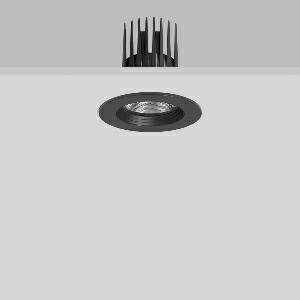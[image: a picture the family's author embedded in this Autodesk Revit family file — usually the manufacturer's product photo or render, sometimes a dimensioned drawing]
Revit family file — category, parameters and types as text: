
# Revit family: heledon_mini_e_901741_003_1376
name_source: partatom
category: Lighting Fixtures
units: mm (PartAtom-declared; Revit-internal decimal feet)

## family parameters
Cut with Voids When Loaded = No
Host = Face
Light Source = No
Part Type = Normal
Room Calculation Point = No
Round Connector Dimension = Use Diameter
Shared = No

## types (1)
- HELEDON mini E (1 x LED Modul 930, 2450 lm, 3000)
    Apparent Load = 20 VA
    Approval mark = CE
    CIE Flux Codes = 99 100 100 100 100
    Color Rendering = 90
    Color Temperature = 3000
    Default Elevation = 1800 mm
    Description = Series: HELEDON mini
Round recessed downlight. Housing: die-cast aluminium, powder-coated. Black plastic ring and recessed LED to prevent glare from the side. Optical assembly with reflector made of MIRO-Silver with 98% total light reflection for outstanding efficiency - can be changed without tools. Best colour rendering index Ra>90. Suitable for Recessed ceiling mounting. Installation without tools thanks to spring fastening system. Including separate LED converter with connecting cable 600 mm.High quality converter without flickering and stroboscopic effect. Through-wiring box (5 pole) available as accessory. The following accessories can be mounted without use of tools: interchangeable lenses, decorative glasses, honeycomb louvre, clear and frosted diffusers, white interchangeable plastic ring. 
Colour: deep black, matt (RAL 9005)
Diameter: 124 mm
Height: 3 mm
Cut-out diameter: 114 mm
Recess height: 170 mm
Luminaire: recess height: 120 mm
Lamp: LED
Socket: without socket
Colour temperature: 3000K
Colour rendering index (CRI): 92
System power: 20 W
Rated luminous flux: 2450 lm
Luminous efficiency: 123 lm/W
Control gear: Regulated power supply
Protection class: II
Type of protection: IP 20
    Height = 0 mm  [stored 0 ft]
    Lamp = 1 x LED Modul 930
    Lamp Light Flux = 2450 lm
    Lamp count = 1
    Length = 124 mm  [stored 0.406824 ft]
    Lifetime = 50000 h
    Luminous efficacy = 123 lm/W
    Manufacturer = RZB
    ModVariant = No
    Model = 901741.003
    Mounting Place = Ceiling
    Mounting Type = Recessed
    Number of Poles = 1
    OnlyDefault = Yes
    Power Factor = 1
    Product Name = HELEDON mini E
    Product group = Recessed downlights
    ProductGroupID = 402
    Protection Class = Protection class II
    Protection Degree = IP 20
    RLX_Detail_Level = 1
    RLX_Emergency_Light_Flux = 0 lm
    RLX_Emergency_Type = 0
    RLX_Emergency_Type_DB = No
    RlxData = <blob elided: 127377 chars, md5=e48d8572>
    Socket = socket
    Standby Power = 0 W
    System Light Flux = 2450 lm
    System Power = 20 W
    Type Comments = Product without accessories
    Type Image = 901657.003.jpg
    URL = http://relux.com
    VarID = ---
    Voltage = 230 V
    Voltage Range = 220-240 V
    Weight = 0.00 kg
    Width = 0 mm  [stored 0 ft]

note: [stored X ft] marks values corroborated as IEEE doubles in the binary element streams (Revit-internal decimal feet)

## geometry (parser evidence)
native form markers: Blend x4, Sweep x12
no freeform markers — native parametric forms only
